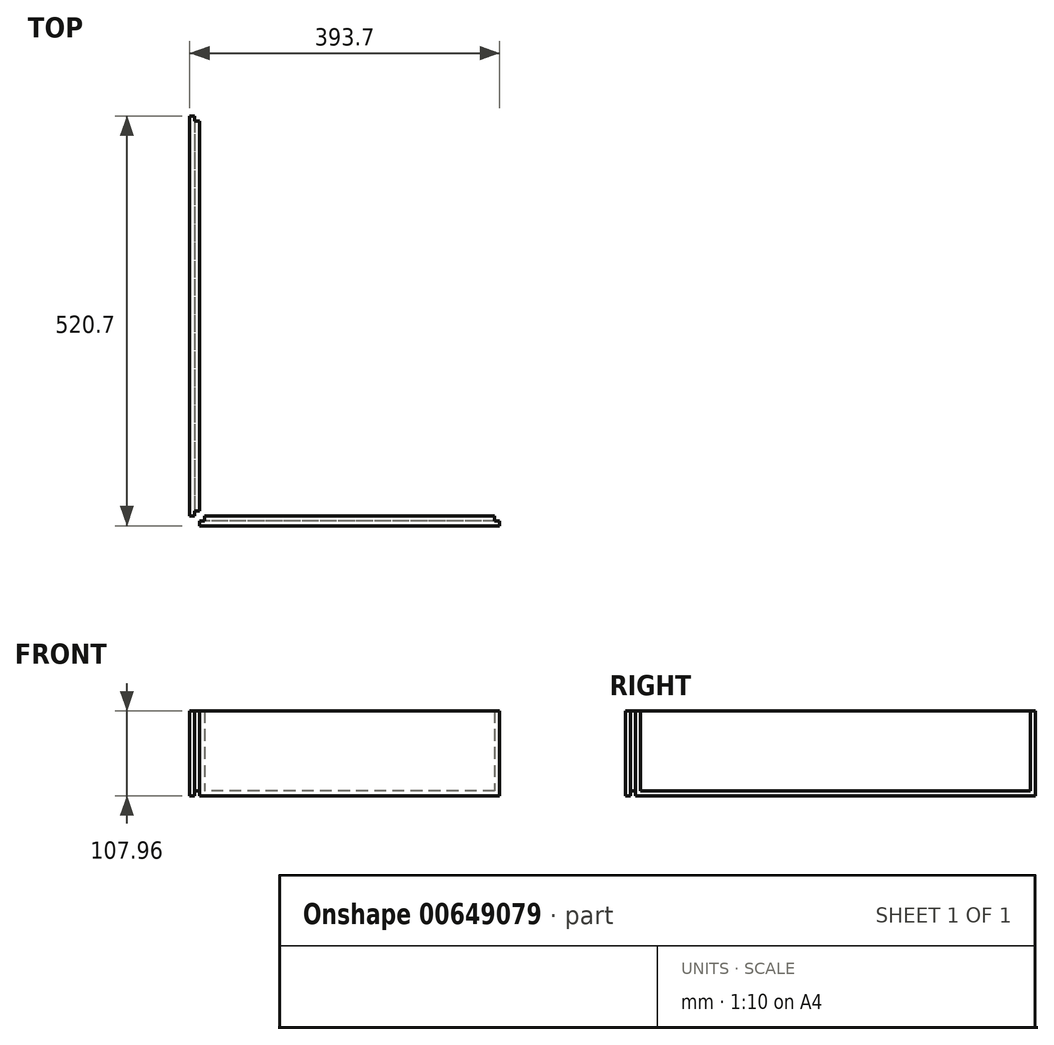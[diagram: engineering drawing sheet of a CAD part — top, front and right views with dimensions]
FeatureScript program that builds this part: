
annotation { "Feature Type Name" : "Feature", "Feature Type Description" : "" }
export const myFeature = defineFeature(function(context is Context, id is Id, definition is map)
    precondition{}
    {
        {
            var Q0;
            Q0=qCreatedBy(makeId("Top.planeOp"),FACE);
            var sketch = newSketch(context, id + "F0", { "sketchPlane" : qUnion([Q0])});
            skLineSegment(sketch, "E0.bottom", {"start": v(-203.2, 254) * mm, "end": v(-196.85, 254) * mm});
            skLineSegment(sketch, "E0.top", {"start": v(-203.2, -254) * mm, "end": v(-196.85, -254) * mm});
            skLineSegment(sketch, "E0.left", {"start": v(-203.2, 254) * mm, "end": v(-203.2, -254) * mm});
            skLineSegment(sketch, "E0.right", {"start": v(-190.5, 247.65) * mm, "end": v(-190.5, -247.65) * mm});
            skLineSegment(sketch, "E1", {"start": v(-196.85, 254) * mm, "end": v(-196.85, 247.65) * mm});
            skLineSegment(sketch, "E2", {"start": v(-196.85, 247.65) * mm, "end": v(-190.5, 247.65) * mm});
            skPoint(sketch, "E3.orphan", {"position": v(-190.5, 254) * mm});
            skLineSegment(sketch, "E4", {"start": v(-196.85, -254) * mm, "end": v(-196.85, -247.65) * mm});
            skLineSegment(sketch, "E5", {"start": v(-196.85, -247.65) * mm, "end": v(-190.5, -247.65) * mm});
            skLineSegment(sketch, "E6", {"start": v(0, 0) * mm, "end": v(-190.5, 0) * mm, "construction": true});
            skSolve(sketch);
        }
        {
            var Q0;
            Q0=makeQuery(id+"F0.imprint","IMPRINT",FACE,{"disambiguationData":[TD([[makeQuery(id+"F0.imprint","IMPRINT",EDGE,{"derivedFrom":sQuery(id+"F0.wireOp",EDGE,"E0.bottom")}),-1.0]])]});
            extrude(context, id + "F1", {"entities" : qUnion([Q0]), "endBound" : BoundingType.SYMMETRIC, "depth" : 107.95 * mm, "offsetDistance" : 25.4 * mm});
        }
        {
            var Q0;
            Q0=qCreatedBy(makeId("Top.planeOp"),FACE);
            var sketch = newSketch(context, id + "F2", { "sketchPlane" : qUnion([Q0])});
            skLineSegment(sketch, "E7.bottom", {"start": v(-184.15, -254) * mm, "end": v(184.15, -254) * mm});
            skLineSegment(sketch, "E7.top", {"start": v(-190.5, -266.7) * mm, "end": v(190.5, -266.7) * mm});
            skLineSegment(sketch, "E7.left", {"start": v(-190.5, -260.35) * mm, "end": v(-190.5, -266.7) * mm});
            skLineSegment(sketch, "E7.right", {"start": v(190.5, -260.35) * mm, "end": v(190.5, -266.7) * mm});
            skLineSegment(sketch, "E8", {"start": v(-190.5, -260.35) * mm, "end": v(-184.15, -260.35) * mm});
            skLineSegment(sketch, "E9", {"start": v(-184.15, -260.35) * mm, "end": v(-184.15, -254) * mm});
            skLineSegment(sketch, "E10", {"start": v(190.5, -260.35) * mm, "end": v(184.15, -260.35) * mm});
            skLineSegment(sketch, "E11", {"start": v(184.15, -260.35) * mm, "end": v(184.15, -254) * mm});
            skLineSegment(sketch, "E12", {"start": v(0, 0) * mm, "end": v(0, -254) * mm, "construction": true});
            skSolve(sketch);
        }
        {
            var Q0;
            Q0=makeQuery(id+"F2.imprint","IMPRINT",FACE,{"disambiguationData":[TD([[makeQuery(id+"F2.imprint","IMPRINT",EDGE,{"derivedFrom":sQuery(id+"F2.wireOp",EDGE,"E7.bottom")}),-1.0]])]});
            extrude(context, id + "F3", {"entities" : qUnion([Q0]), "endBound" : BoundingType.SYMMETRIC, "depth" : 107.95 * mm, "offsetDistance" : 25.4 * mm});
        }
        {
            var Q0;
            Q0=makeQuery(id+"F1.opExtrude","SWEPT_FACE",FACE,{"disambiguationData":[OSD([sQuery(id+"F0.wireOp",EDGE,"E0.right")])]});
            var sketch = newSketch(context, id + "F4", { "sketchPlane" : qUnion([Q0])});
            skLineSegment(sketch, "E13.bottom", {"start": v(247.65, -53.98) * mm, "end": v(-247.65, -53.98) * mm});
            skLineSegment(sketch, "E13.top", {"start": v(247.65, -47.62) * mm, "end": v(-247.65, -47.63) * mm});
            skLineSegment(sketch, "E13.left", {"start": v(247.65, -53.98) * mm, "end": v(247.65, -47.62) * mm});
            skLineSegment(sketch, "E13.right", {"start": v(-247.65, -53.98) * mm, "end": v(-247.65, -47.63) * mm});
            skSolve(sketch);
        }
        {
            var Q0;
            Q0 = qSketchRegion(id + "F4", true);
            var Q1;
            Q1=makeQuery(id+"F1.opExtrude","SWEPT_FACE",FACE,{"disambiguationData":[OSD([sQuery(id+"F0.wireOp",EDGE,"E4")])]});
            extrude(context, id + "F5", {"entities" : qUnion([Q0]), "operationType" : NewBodyOperationType.REMOVE, "endBound" : BoundingType.UP_TO_SURFACE, "oppositeDirection" : true, "depth" : 25.4 * mm, "endBoundEntityFace" : qUnion([Q1]), "offsetDistance" : 25.4 * mm});
        }
        {
            var Q0;
            Q0=makeQuery(id+"F3.opExtrude","SWEPT_FACE",FACE,{"disambiguationData":[OSD([sQuery(id+"F2.wireOp",EDGE,"E7.bottom")])]});
            var sketch = newSketch(context, id + "F6", { "sketchPlane" : qUnion([Q0])});
            skLineSegment(sketch, "E14.bottom", {"start": v(-184.15, -53.98) * mm, "end": v(184.15, -53.98) * mm});
            skLineSegment(sketch, "E14.top", {"start": v(-184.15, -47.63) * mm, "end": v(184.15, -47.63) * mm});
            skLineSegment(sketch, "E14.left", {"start": v(-184.15, -53.98) * mm, "end": v(-184.15, -47.63) * mm});
            skLineSegment(sketch, "E14.right", {"start": v(184.15, -53.98) * mm, "end": v(184.15, -47.63) * mm});
            skSolve(sketch);
        }
        {
            var Q0;
            Q0 = qSketchRegion(id + "F6", true);
            var Q1;
            Q1=makeQuery(id+"F3.opExtrude","SWEPT_FACE",FACE,{"disambiguationData":[OSD([sQuery(id+"F2.wireOp",EDGE,"E10")])]});
            extrude(context, id + "F7", {"entities" : qUnion([Q0]), "operationType" : NewBodyOperationType.REMOVE, "endBound" : BoundingType.UP_TO_SURFACE, "oppositeDirection" : true, "depth" : 25.4 * mm, "endBoundEntityFace" : qUnion([Q1]), "offsetDistance" : 25.4 * mm});
        }
    });
